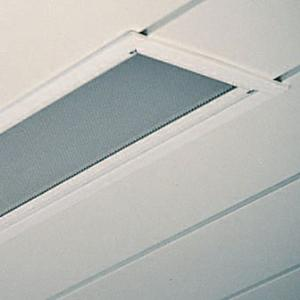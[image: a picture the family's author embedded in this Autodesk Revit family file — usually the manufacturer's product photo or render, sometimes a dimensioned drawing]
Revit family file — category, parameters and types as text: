
# Revit family: 3f_filippi_-_l_560_sp_3f_filippi_-_270965_-_l_562x24w_led_sp_221x1256
name_source: partatom
category: Lighting Fixtures
units: mm (PartAtom-declared; Revit-internal decimal feet)

## family parameters
Cut with Voids When Loaded = No
Host = Face
Light Source = No
Part Type = Normal
Room Calculation Point = No
Round Connector Dimension = Use Diameter
Shared = No

## types (1)
- 3F Filippi - L 560 SP (1 x LED, 5755 lm, 54 W, 4000 K)
    Apparent Load = 54 VA
    Approval mark = ENEC
    CIE Flux Codes = 64 90 98 100 100
    Color Rendering = 80
    Color Temperature = 4000 K
    Control Gear = Electronic ballast
    Default Elevation = 1800 mm
    Description = ILLUMINOTECHNICAL
Luminous efficiency 100% (DLOR 100%, ULOR 0%).
Initial luminous flux of the luminaire 5755 lm.
Direct symmetric distribution.
Installation Interdistance Transv.D = 1.03 x hu - Long.D = 1.18 x hu.
Tabular UGR (CIE 117 - 4H-8H; S=0.25H; 70/50/20): RUG 20.2 - 22.1.
Beam angle: 74° - 94°.
Luminous efficacy 107 lm/W.
Lifetime (L93/B10): 30000 h. (tq+25°C)
Lifetime (L90/B10): 50000 h. (tq+25°C)
Lifetime (L85/B10): 80000 h. (tq+25°C)
Lifetime (L80/B10): 100000 h. (tq+25°C)
Sudden decreased luminous flux after 50000 hours: 0% (C0).
Photobiological safety in compliance with IEC/TR 62778: RG0 risk exempt, (IEC 62471).
In compliance with IEC/EN 62722-2-1 - IEC/EN 62717 standards.

SOURCE
2 linear LED modules 24W/840.
Energy efficiency class (UE 2019/2020 - UE 2019/2015): D.
CIE 13.3 Colour rendering index: CRI >80 (R9 <50%).
IES TM-30 Fidelity Index: Rf = 84 Rg = 95.
CCT nominal colour temperature 4000 K.
Colour initial tolerance (MacAdam): SDCM 3.

MECHANICAL
Housing in galvannealed steel, painted in white epoxy-polyester.
SP transparent methacrylate (PMMA) flat diffuser, externally multilenticular, anti-glare, injection moulded, locked to the white painted aluminium perimetrical frame, hinged opening.
Luminaire with limited surface temperature. - D - (EN 60598-2-24)
Dimensions: 1256x221 mm, height 95 mm. Weight 5.205 kg.
IP54 protection degree for exposed part, IP20 for recessed part.
Mechanical strength to impacts IK06 (1 joule).
Glow-wire test resistance 650°C.

ELECTRICAL
Halogen Free electronic wiring 230V-50/60Hz, power factor 0.95, THD <25%, constant output current, SELV, class I, 1 driver.
Power of the luminaire 54 W.
CE - IEC 60598-1 - EN 60598-1.
SAFE FLICKER: PstLM=<1 and SVM=<0.4 (IEC TR 61547-1 and IEC TR 63158), to ensure a more comfortable and safe light.
Luminaire compliant with EN 60598-2-22 for power supply from a centralised emergency system CPSS (Central Power Supply System), not incorporated in the luminaire - high risk areas excluded. The default power and flux are 100% in AC and 100% in DC.
Ambient temperature from 0°C to +25°C.
Temperature class T6 max 85°C.
Relative humidity UR: <85%.

INSTALLATION
Pull-up recessed fitting / Slat ceiling recessed fitting.
False ceiling carving: 190x1230 mm.
All accessories dedicated to this product are available on the Catalog and on our website www.3F-Filippi.com.

APPLICATIONS
Suitable product for food production plants (HACCP), IFS (Food Version 6), BRC (GSFS Food Version 7).
Recessed installation in environments requiring protection, good visual comfort with lamp shielding and simplified cleaning.

WARNING
Luminaire designed for disposal/recycling at end-of-life.
Replaceable (LED only) light source by a professional. Replaceable control gear by a professional.
    Height = 0 mm  [stored 0 ft]
    Lamp = 1 x LED
    Lamp Light Flux = 5755 lm
    Lamp Power = 54 W
    Lamp count = 1
    Length = 1256 mm
    Lifetime = 50000 h
    Luminous efficacy = 107 lm/W
    Manufacturer = 3F Filippi
    ModVariant = No
    Model = 3F Filippi - 270965 - L 562x24W LED SP 221x1256
    Mounting Place = Ceiling
    Mounting Type = Recessed
    Number of Poles = 1
    OnlyDefault = Yes
    Power Factor = 1
    Product Name = 3F Filippi - L 560 SP
    Product group = recessed luminaire
    ProductGroupID = 4
    Protection Class = Protection class I
    Protection Degree = IP 20
    RLX_Detail_Level = 1
    RLX_Emergency_Light_Flux = 0 lm
    RLX_Emergency_Type = 0
    RLX_Emergency_Type_DB = No
    RlxData = <blob elided: 84273 chars, md5=f5881523>
    Socket = socket
    Standby Power = 0 W
    System Light Flux = 5755 lm
    System Power = 54 W
    Type Comments = Product without accessories
    Type Image = 3ffilippi_270965.jpg
    URL = http://relux.com
    VarID = ---
    Voltage = 0 V
    Weight = 0.00 kg
    Width = 221 mm

note: [stored X ft] marks values corroborated as IEEE doubles in the binary element streams (Revit-internal decimal feet)

## geometry (parser evidence)
native form markers: Blend x4, Sweep x10
no freeform markers — native parametric forms only
